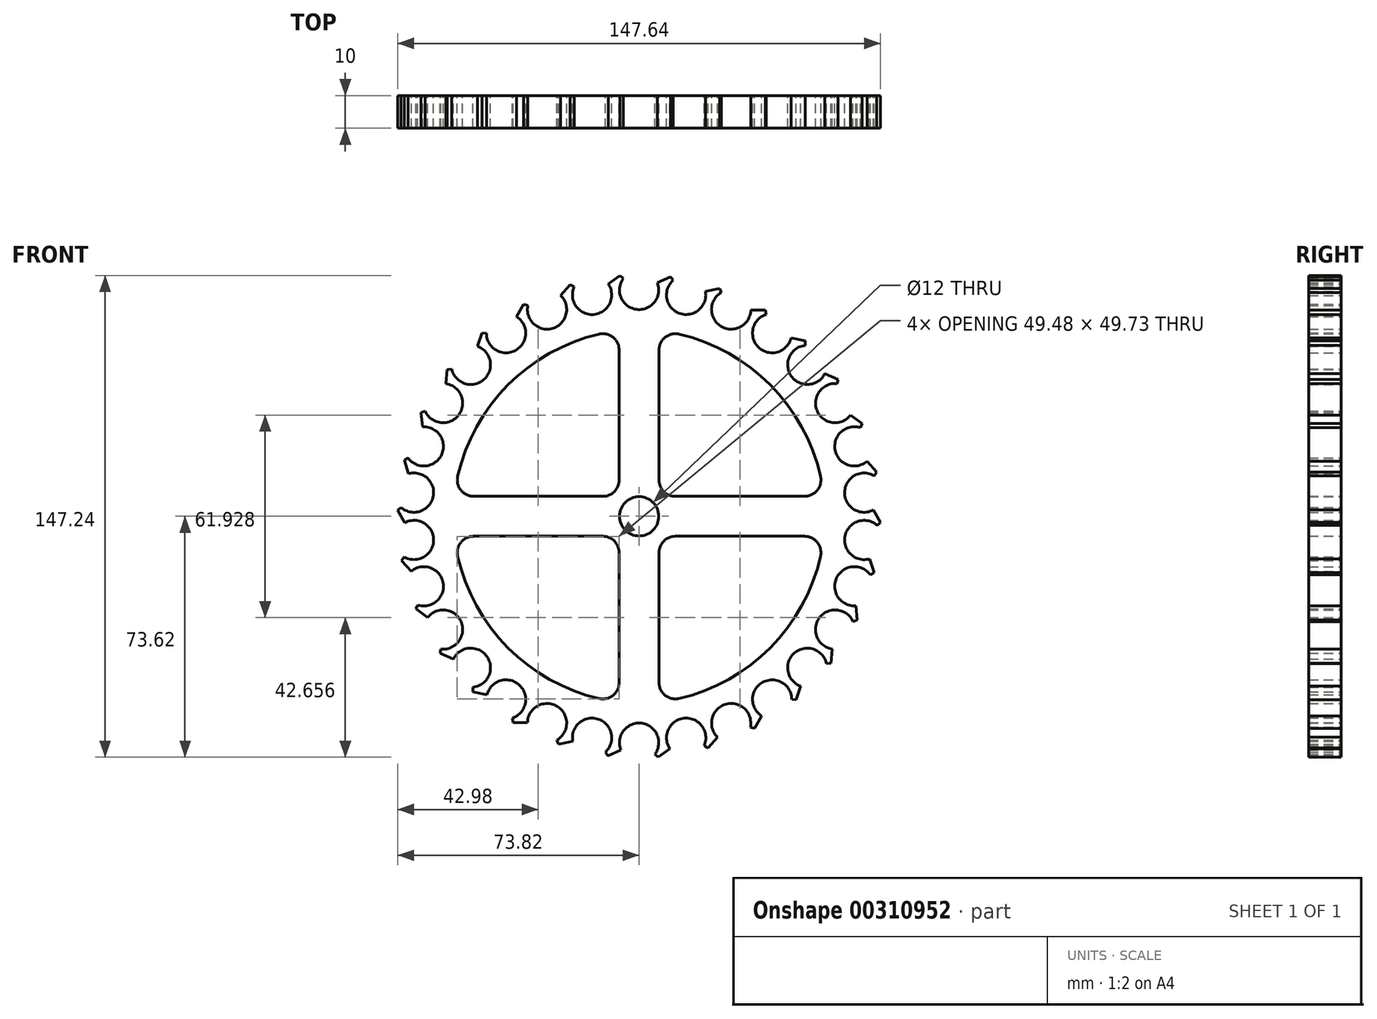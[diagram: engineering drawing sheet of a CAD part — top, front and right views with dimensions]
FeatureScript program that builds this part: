
annotation { "Feature Type Name" : "Feature", "Feature Type Description" : "" }
export const myFeature = defineFeature(function(context is Context, id is Id, definition is map)
    precondition{}
    {
        {
            var Q0;
            Q0=qCreatedBy(makeId("Front.planeOp"),FACE);
            var sketch = newSketch(context, id + "F0", { "sketchPlane" : qUnion([Q0])});
            skArc(sketch, "E0", {"start": v(10.36, 72.14) * mm, "mid": v(8.6, 66.13) * mm, "end": v(13.14, 61.82) * mm});
            skLineSegment(sketch, "E1", {"start": v(10.36, 72.14) * mm, "end": v(9.57, 73.23) * mm});
            skLineSegment(sketch, "E2.trimOffspring", {"start": v(9.57, 73.23) * mm, "end": v(5.57, 71.44) * mm});
            skArc(sketch, "E3.trimOffspring", {"start": v(0, 63.2) * mm, "mid": v(4.97, 65.84) * mm, "end": v(5.57, 71.44) * mm});
            skArc(sketch, "E4.1.0", {"start": v(-13.14, 61.82) * mm, "mid": v(-8.83, 65.44) * mm, "end": v(-9.4, 71.04) * mm});
            skLineSegment(sketch, "E4.1.1", {"start": v(-5.86, 73.62) * mm, "end": v(-9.4, 71.04) * mm});
            skLineSegment(sketch, "E4.1.2", {"start": v(-4.86, 72.72) * mm, "end": v(-5.86, 73.62) * mm});
            skArc(sketch, "E4.1.3", {"start": v(-4.86, 72.72) * mm, "mid": v(-5.34, 66.47) * mm, "end": v(0, 63.2) * mm});
            skArc(sketch, "E4.2.0", {"start": v(-25.7, 57.74) * mm, "mid": v(-22.24, 62.17) * mm, "end": v(-23.97, 67.53) * mm});
            skLineSegment(sketch, "E4.2.1", {"start": v(-21.04, 70.79) * mm, "end": v(-23.97, 67.53) * mm});
            skLineSegment(sketch, "E4.2.2", {"start": v(-19.87, 70.12) * mm, "end": v(-21.04, 70.79) * mm});
            skArc(sketch, "E4.2.3", {"start": v(-19.87, 70.12) * mm, "mid": v(-19.05, 63.9) * mm, "end": v(-13.14, 61.82) * mm});
            skPoint(sketch, "E4.center", {"position": v(0, 0) * mm});
            skArc(sketch, "E5.2.3.0", {"start": v(-37.15, 51.13) * mm, "mid": v(-34.68, 56.19) * mm, "end": v(-37.49, 61.07) * mm});
            skLineSegment(sketch, "E5.4.3.0", {"start": v(-35.3, 64.87) * mm, "end": v(-37.49, 61.07) * mm});
            skLineSegment(sketch, "E5.7.3.0", {"start": v(-34.02, 64.45) * mm, "end": v(-35.3, 64.87) * mm});
            skArc(sketch, "E5.10.3.0", {"start": v(-34.02, 64.45) * mm, "mid": v(-31.92, 58.55) * mm, "end": v(-25.7, 57.74) * mm});
            skArc(sketch, "E5.2.4.0", {"start": v(-46.97, 42.29) * mm, "mid": v(-45.6, 47.75) * mm, "end": v(-49.37, 51.94) * mm});
            skLineSegment(sketch, "E5.4.4.0", {"start": v(-48.01, 56.11) * mm, "end": v(-49.37, 51.94) * mm});
            skLineSegment(sketch, "E5.7.4.0", {"start": v(-46.67, 55.97) * mm, "end": v(-48.01, 56.11) * mm});
            skArc(sketch, "E5.10.4.0", {"start": v(-46.67, 55.97) * mm, "mid": v(-43.4, 50.64) * mm, "end": v(-37.15, 51.13) * mm});
            skArc(sketch, "E5.2.5.0", {"start": v(-54.73, 31.6) * mm, "mid": v(-54.53, 37.23) * mm, "end": v(-59.09, 40.54) * mm});
            skLineSegment(sketch, "E5.4.5.0", {"start": v(-58.63, 44.9) * mm, "end": v(-59.09, 40.54) * mm});
            skLineSegment(sketch, "E5.7.5.0", {"start": v(-57.3, 45.04) * mm, "end": v(-58.63, 44.9) * mm});
            skArc(sketch, "E5.10.5.0", {"start": v(-57.3, 45.04) * mm, "mid": v(-52.97, 40.5) * mm, "end": v(-46.97, 42.29) * mm});
            skArc(sketch, "E5.2.6.0", {"start": v(-60.1, 19.53) * mm, "mid": v(-61.08, 25.08) * mm, "end": v(-66.22, 27.37) * mm});
            skLineSegment(sketch, "E5.4.6.0", {"start": v(-66.68, 31.73) * mm, "end": v(-66.22, 27.37) * mm});
            skLineSegment(sketch, "E5.7.6.0", {"start": v(-65.4, 32.15) * mm, "end": v(-66.68, 31.73) * mm});
            skArc(sketch, "E5.10.6.0", {"start": v(-65.4, 32.15) * mm, "mid": v(-60.24, 28.6) * mm, "end": v(-54.73, 31.6) * mm});
            skArc(sketch, "E5.2.7.0", {"start": v(-62.85, 6.6) * mm, "mid": v(-64.96, 11.83) * mm, "end": v(-70.47, 13) * mm});
            skLineSegment(sketch, "E5.4.7.0", {"start": v(-71.82, 17.18) * mm, "end": v(-70.47, 13) * mm});
            skLineSegment(sketch, "E5.7.7.0", {"start": v(-70.66, 17.85) * mm, "end": v(-71.82, 17.18) * mm});
            skArc(sketch, "E5.10.7.0", {"start": v(-70.66, 17.85) * mm, "mid": v(-64.87, 15.46) * mm, "end": v(-60.1, 19.53) * mm});
            skArc(sketch, "E5.2.8.0", {"start": v(-62.85, -6.6) * mm, "mid": v(-66, -1.94) * mm, "end": v(-71.63, -1.93) * mm});
            skLineSegment(sketch, "E5.4.8.0", {"start": v(-73.82, 1.87) * mm, "end": v(-71.63, -1.93) * mm});
            skLineSegment(sketch, "E5.7.8.0", {"start": v(-72.83, 2.77) * mm, "end": v(-73.82, 1.87) * mm});
            skArc(sketch, "E5.10.8.0", {"start": v(-72.83, 2.77) * mm, "mid": v(-66.66, 1.63) * mm, "end": v(-62.85, 6.6) * mm});
            skArc(sketch, "E5.2.9.0", {"start": v(-60.1, -19.53) * mm, "mid": v(-64.16, -15.62) * mm, "end": v(-69.66, -16.78) * mm});
            skLineSegment(sketch, "E5.4.9.0", {"start": v(-72.6, -13.52) * mm, "end": v(-69.66, -16.78) * mm});
            skLineSegment(sketch, "E5.7.9.0", {"start": v(-71.8, -12.44) * mm, "end": v(-72.6, -13.52) * mm});
            skArc(sketch, "E5.10.9.0", {"start": v(-71.8, -12.44) * mm, "mid": v(-65.55, -12.26) * mm, "end": v(-62.85, -6.6) * mm});
            skArc(sketch, "E5.2.10.0", {"start": v(-54.73, -31.6) * mm, "mid": v(-59.5, -28.61) * mm, "end": v(-64.65, -30.9) * mm});
            skLineSegment(sketch, "E5.4.10.0", {"start": v(-68.2, -28.32) * mm, "end": v(-64.65, -30.9) * mm});
            skLineSegment(sketch, "E5.7.10.0", {"start": v(-67.66, -27.1) * mm, "end": v(-68.2, -28.32) * mm});
            skArc(sketch, "E5.10.10.0", {"start": v(-67.66, -27.1) * mm, "mid": v(-61.57, -25.62) * mm, "end": v(-60.1, -19.53) * mm});
            skArc(sketch, "E5.2.11.0", {"start": v(-46.97, -42.29) * mm, "mid": v(-52.26, -40.36) * mm, "end": v(-56.82, -43.67) * mm});
            skLineSegment(sketch, "E5.4.11.0", {"start": v(-60.82, -41.88) * mm, "end": v(-56.82, -43.67) * mm});
            skLineSegment(sketch, "E5.7.11.0", {"start": v(-60.54, -40.57) * mm, "end": v(-60.82, -41.88) * mm});
            skArc(sketch, "E5.10.11.0", {"start": v(-60.54, -40.57) * mm, "mid": v(-54.9, -37.86) * mm, "end": v(-54.73, -31.6) * mm});
            skArc(sketch, "E5.2.12.0", {"start": v(-37.15, -51.13) * mm, "mid": v(-42.72, -50.34) * mm, "end": v(-46.5, -54.53) * mm});
            skLineSegment(sketch, "E5.4.12.0", {"start": v(-50.79, -53.61) * mm, "end": v(-46.5, -54.53) * mm});
            skLineSegment(sketch, "E5.7.12.0", {"start": v(-50.79, -52.27) * mm, "end": v(-50.79, -53.61) * mm});
            skArc(sketch, "E5.10.12.0", {"start": v(-50.79, -52.27) * mm, "mid": v(-45.82, -48.45) * mm, "end": v(-46.97, -42.29) * mm});
            skArc(sketch, "E5.2.13.0", {"start": v(-25.7, -57.74) * mm, "mid": v(-31.32, -58.13) * mm, "end": v(-34.14, -63) * mm});
            skLineSegment(sketch, "E5.4.13.0", {"start": v(-38.53, -63) * mm, "end": v(-34.14, -63) * mm});
            skLineSegment(sketch, "E5.7.13.0", {"start": v(-38.8, -61.69) * mm, "end": v(-38.53, -63) * mm});
            skArc(sketch, "E5.10.13.0", {"start": v(-38.8, -61.69) * mm, "mid": v(-34.75, -56.92) * mm, "end": v(-37.15, -51.13) * mm});
            skArc(sketch, "E5.2.14.0", {"start": v(-13.14, -61.82) * mm, "mid": v(-18.55, -63.37) * mm, "end": v(-20.3, -68.72) * mm});
            skLineSegment(sketch, "E5.4.14.0", {"start": v(-24.59, -69.63) * mm, "end": v(-20.3, -68.72) * mm});
            skLineSegment(sketch, "E5.7.14.0", {"start": v(-25.14, -68.4) * mm, "end": v(-24.59, -69.63) * mm});
            skArc(sketch, "E5.10.14.0", {"start": v(-25.14, -68.4) * mm, "mid": v(-22.15, -62.9) * mm, "end": v(-25.7, -57.74) * mm});
            skArc(sketch, "E5.2.15.0", {"start": v(0, -63.2) * mm, "mid": v(-4.97, -65.84) * mm, "end": v(-5.57, -71.44) * mm});
            skLineSegment(sketch, "E5.4.15.0", {"start": v(-9.57, -73.23) * mm, "end": v(-5.57, -71.44) * mm});
            skLineSegment(sketch, "E5.7.15.0", {"start": v(-10.36, -72.14) * mm, "end": v(-9.57, -73.23) * mm});
            skArc(sketch, "E5.10.15.0", {"start": v(-10.36, -72.14) * mm, "mid": v(-8.6, -66.13) * mm, "end": v(-13.14, -61.82) * mm});
            skArc(sketch, "E5.2.16.0", {"start": v(13.14, -61.82) * mm, "mid": v(8.83, -65.44) * mm, "end": v(9.4, -71.04) * mm});
            skLineSegment(sketch, "E5.4.16.0", {"start": v(5.86, -73.62) * mm, "end": v(9.4, -71.04) * mm});
            skLineSegment(sketch, "E5.7.16.0", {"start": v(4.86, -72.72) * mm, "end": v(5.86, -73.62) * mm});
            skArc(sketch, "E5.10.16.0", {"start": v(4.86, -72.72) * mm, "mid": v(5.34, -66.47) * mm, "end": v(0, -63.2) * mm});
            skArc(sketch, "E5.2.17.0", {"start": v(25.7, -57.74) * mm, "mid": v(22.24, -62.17) * mm, "end": v(23.97, -67.53) * mm});
            skLineSegment(sketch, "E5.4.17.0", {"start": v(21.04, -70.79) * mm, "end": v(23.97, -67.53) * mm});
            skLineSegment(sketch, "E5.7.17.0", {"start": v(19.87, -70.12) * mm, "end": v(21.04, -70.79) * mm});
            skArc(sketch, "E5.10.17.0", {"start": v(19.87, -70.12) * mm, "mid": v(19.05, -63.9) * mm, "end": v(13.14, -61.82) * mm});
            skArc(sketch, "E5.2.18.0", {"start": v(37.15, -51.13) * mm, "mid": v(34.68, -56.19) * mm, "end": v(37.49, -61.07) * mm});
            skLineSegment(sketch, "E5.4.18.0", {"start": v(35.3, -64.87) * mm, "end": v(37.49, -61.07) * mm});
            skLineSegment(sketch, "E5.7.18.0", {"start": v(34.02, -64.45) * mm, "end": v(35.3, -64.87) * mm});
            skArc(sketch, "E5.10.18.0", {"start": v(34.02, -64.45) * mm, "mid": v(31.92, -58.55) * mm, "end": v(25.7, -57.74) * mm});
            skArc(sketch, "E5.2.19.0", {"start": v(46.97, -42.29) * mm, "mid": v(45.6, -47.75) * mm, "end": v(49.37, -51.94) * mm});
            skLineSegment(sketch, "E5.4.19.0", {"start": v(48.01, -56.11) * mm, "end": v(49.37, -51.94) * mm});
            skLineSegment(sketch, "E5.7.19.0", {"start": v(46.67, -55.97) * mm, "end": v(48.01, -56.11) * mm});
            skArc(sketch, "E5.10.19.0", {"start": v(46.67, -55.97) * mm, "mid": v(43.4, -50.64) * mm, "end": v(37.15, -51.13) * mm});
            skArc(sketch, "E5.2.20.0", {"start": v(54.73, -31.6) * mm, "mid": v(54.53, -37.23) * mm, "end": v(59.09, -40.54) * mm});
            skLineSegment(sketch, "E5.4.20.0", {"start": v(58.63, -44.9) * mm, "end": v(59.09, -40.54) * mm});
            skLineSegment(sketch, "E5.7.20.0", {"start": v(57.3, -45.04) * mm, "end": v(58.63, -44.9) * mm});
            skArc(sketch, "E5.10.20.0", {"start": v(57.3, -45.04) * mm, "mid": v(52.97, -40.5) * mm, "end": v(46.97, -42.29) * mm});
            skArc(sketch, "E5.2.21.0", {"start": v(60.1, -19.53) * mm, "mid": v(61.08, -25.08) * mm, "end": v(66.22, -27.37) * mm});
            skLineSegment(sketch, "E5.4.21.0", {"start": v(66.68, -31.73) * mm, "end": v(66.22, -27.37) * mm});
            skLineSegment(sketch, "E5.7.21.0", {"start": v(65.4, -32.15) * mm, "end": v(66.68, -31.73) * mm});
            skArc(sketch, "E5.10.21.0", {"start": v(65.4, -32.15) * mm, "mid": v(60.24, -28.6) * mm, "end": v(54.73, -31.6) * mm});
            skArc(sketch, "E5.2.22.0", {"start": v(62.85, -6.6) * mm, "mid": v(64.96, -11.83) * mm, "end": v(70.47, -13) * mm});
            skLineSegment(sketch, "E5.4.22.0", {"start": v(71.82, -17.18) * mm, "end": v(70.47, -13) * mm});
            skLineSegment(sketch, "E5.7.22.0", {"start": v(70.66, -17.85) * mm, "end": v(71.82, -17.18) * mm});
            skArc(sketch, "E5.10.22.0", {"start": v(70.66, -17.85) * mm, "mid": v(64.87, -15.46) * mm, "end": v(60.1, -19.53) * mm});
            skArc(sketch, "E5.2.23.0", {"start": v(62.85, 6.6) * mm, "mid": v(66, 1.94) * mm, "end": v(71.63, 1.93) * mm});
            skLineSegment(sketch, "E5.4.23.0", {"start": v(73.82, -1.87) * mm, "end": v(71.63, 1.93) * mm});
            skLineSegment(sketch, "E5.7.23.0", {"start": v(72.83, -2.77) * mm, "end": v(73.82, -1.87) * mm});
            skArc(sketch, "E5.10.23.0", {"start": v(72.83, -2.77) * mm, "mid": v(66.66, -1.63) * mm, "end": v(62.85, -6.6) * mm});
            skArc(sketch, "E5.2.24.0", {"start": v(60.1, 19.53) * mm, "mid": v(64.16, 15.62) * mm, "end": v(69.66, 16.78) * mm});
            skLineSegment(sketch, "E5.4.24.0", {"start": v(72.6, 13.52) * mm, "end": v(69.66, 16.78) * mm});
            skLineSegment(sketch, "E5.7.24.0", {"start": v(71.8, 12.44) * mm, "end": v(72.6, 13.52) * mm});
            skArc(sketch, "E5.10.24.0", {"start": v(71.8, 12.44) * mm, "mid": v(65.55, 12.26) * mm, "end": v(62.85, 6.6) * mm});
            skArc(sketch, "E5.2.25.0", {"start": v(54.73, 31.6) * mm, "mid": v(59.5, 28.61) * mm, "end": v(64.65, 30.9) * mm});
            skLineSegment(sketch, "E5.4.25.0", {"start": v(68.2, 28.32) * mm, "end": v(64.65, 30.9) * mm});
            skLineSegment(sketch, "E5.7.25.0", {"start": v(67.66, 27.1) * mm, "end": v(68.2, 28.32) * mm});
            skArc(sketch, "E5.10.25.0", {"start": v(67.66, 27.1) * mm, "mid": v(61.57, 25.62) * mm, "end": v(60.1, 19.53) * mm});
            skArc(sketch, "E5.2.26.0", {"start": v(46.97, 42.29) * mm, "mid": v(52.26, 40.36) * mm, "end": v(56.82, 43.67) * mm});
            skLineSegment(sketch, "E5.4.26.0", {"start": v(60.82, 41.88) * mm, "end": v(56.82, 43.67) * mm});
            skLineSegment(sketch, "E5.7.26.0", {"start": v(60.54, 40.57) * mm, "end": v(60.82, 41.88) * mm});
            skArc(sketch, "E5.10.26.0", {"start": v(60.54, 40.57) * mm, "mid": v(54.9, 37.86) * mm, "end": v(54.73, 31.6) * mm});
            skArc(sketch, "E5.2.27.0", {"start": v(37.15, 51.13) * mm, "mid": v(42.72, 50.34) * mm, "end": v(46.5, 54.53) * mm});
            skLineSegment(sketch, "E5.4.27.0", {"start": v(50.79, 53.61) * mm, "end": v(46.5, 54.53) * mm});
            skLineSegment(sketch, "E5.7.27.0", {"start": v(50.79, 52.27) * mm, "end": v(50.79, 53.61) * mm});
            skArc(sketch, "E5.10.27.0", {"start": v(50.79, 52.27) * mm, "mid": v(45.82, 48.45) * mm, "end": v(46.97, 42.29) * mm});
            skArc(sketch, "E5.2.28.0", {"start": v(25.7, 57.74) * mm, "mid": v(31.32, 58.13) * mm, "end": v(34.14, 63) * mm});
            skLineSegment(sketch, "E5.4.28.0", {"start": v(38.53, 63) * mm, "end": v(34.14, 63) * mm});
            skLineSegment(sketch, "E5.7.28.0", {"start": v(38.8, 61.69) * mm, "end": v(38.53, 63) * mm});
            skArc(sketch, "E5.10.28.0", {"start": v(38.8, 61.69) * mm, "mid": v(34.75, 56.92) * mm, "end": v(37.15, 51.13) * mm});
            skArc(sketch, "E5.2.29.0", {"start": v(13.14, 61.82) * mm, "mid": v(18.55, 63.37) * mm, "end": v(20.3, 68.72) * mm});
            skLineSegment(sketch, "E5.4.29.0", {"start": v(24.59, 69.63) * mm, "end": v(20.3, 68.72) * mm});
            skLineSegment(sketch, "E5.7.29.0", {"start": v(25.14, 68.4) * mm, "end": v(24.59, 69.63) * mm});
            skArc(sketch, "E5.10.29.0", {"start": v(25.14, 68.4) * mm, "mid": v(22.15, 62.9) * mm, "end": v(25.7, 57.74) * mm});
            skCircle(sketch, "E6", {"center": v(0, 0) * mm, "radius": 6 * mm});
            skSolve(sketch);
        }
        {
            var Q0;
            Q0=makeQuery(id+"F0.imprint","IMPRINT",FACE,{"disambiguationData":[TD([[makeQuery(id+"F0.imprint","IMPRINT",EDGE,{"derivedFrom":sQuery(id+"F0.wireOp",EDGE,"E0")}),-1.0]])]});
            extrude(context, id + "F1", {"entities" : qUnion([Q0]), "depth" : 10 * mm});
        }
        {
            var Q0;
            Q0=qCreatedBy(makeId("Front.planeOp"),FACE);
            var sketch = newSketch(context, id + "F2", { "sketchPlane" : qUnion([Q0])});
            skLineSegment(sketch, "E7", {"start": v(0, 0) * mm, "end": v(0, 72.45) * mm});
            skLineSegment(sketch, "E8", {"start": v(0, 0) * mm, "end": v(-82.84, 0) * mm});
            skArc(sketch, "E9.0", {"start": v(-12.23, 55.7) * mm, "mid": v(-40.1, 40.17) * mm, "end": v(-55.46, 12.2) * mm});
            skLineSegment(sketch, "E10.0", {"start": v(-6.1, 11.1) * mm, "end": v(-6.1, 50.83) * mm});
            skLineSegment(sketch, "E11.0", {"start": v(-11.1, 6.1) * mm, "end": v(-50.58, 6.1) * mm});
            skArc(sketch, "E12.filletArc", {"start": v(-11.1, 6.1) * mm, "mid": v(-7.56, 7.56) * mm, "end": v(-6.1, 11.1) * mm});
            skArc(sketch, "E13.filletArc", {"start": v(-6.1, 50.83) * mm, "mid": v(-7.99, 54.74) * mm, "end": v(-12.23, 55.7) * mm});
            skArc(sketch, "E14.filletArc", {"start": v(-55.46, 12.2) * mm, "mid": v(-54.49, 7.98) * mm, "end": v(-50.58, 6.1) * mm});
            skArc(sketch, "E15.MirrorCS", {"start": v(12.23, 55.7) * mm, "mid": v(40.1, 40.17) * mm, "end": v(55.46, 12.2) * mm});
            skArc(sketch, "E16.MirrorCS", {"start": v(6.1, 50.83) * mm, "mid": v(7.99, 54.74) * mm, "end": v(12.23, 55.7) * mm});
            skLineSegment(sketch, "E17.MirrorCS", {"start": v(6.1, 11.1) * mm, "end": v(6.1, 50.83) * mm});
            skArc(sketch, "E18.MirrorCS", {"start": v(11.1, 6.1) * mm, "mid": v(7.56, 7.56) * mm, "end": v(6.1, 11.1) * mm});
            skLineSegment(sketch, "E19.MirrorCS", {"start": v(11.1, 6.1) * mm, "end": v(50.58, 6.1) * mm});
            skArc(sketch, "E20.MirrorCS", {"start": v(55.46, 12.2) * mm, "mid": v(54.49, 7.98) * mm, "end": v(50.58, 6.1) * mm});
            skLineSegment(sketch, "E21.MirrorCS", {"start": v(-11.1, -6.1) * mm, "end": v(-50.58, -6.1) * mm});
            skArc(sketch, "E22.MirrorCS", {"start": v(-11.1, -6.1) * mm, "mid": v(-7.56, -7.56) * mm, "end": v(-6.1, -11.1) * mm});
            skLineSegment(sketch, "E23.MirrorCS", {"start": v(-6.1, -11.1) * mm, "end": v(-6.1, -50.83) * mm});
            skArc(sketch, "E24.MirrorCS", {"start": v(-6.1, -50.83) * mm, "mid": v(-7.99, -54.74) * mm, "end": v(-12.23, -55.7) * mm});
            skArc(sketch, "E25.MirrorCS", {"start": v(-12.23, -55.7) * mm, "mid": v(-40.1, -40.17) * mm, "end": v(-55.46, -12.2) * mm});
            skArc(sketch, "E26.MirrorCS", {"start": v(-55.46, -12.2) * mm, "mid": v(-54.49, -7.98) * mm, "end": v(-50.58, -6.1) * mm});
            skLineSegment(sketch, "E27.MirrorCS", {"start": v(11.1, -6.1) * mm, "end": v(50.58, -6.1) * mm});
            skArc(sketch, "E28.MirrorCS", {"start": v(11.1, -6.1) * mm, "mid": v(7.56, -7.56) * mm, "end": v(6.1, -11.1) * mm});
            skLineSegment(sketch, "E29.MirrorCS", {"start": v(6.1, -11.1) * mm, "end": v(6.1, -50.83) * mm});
            skArc(sketch, "E30.MirrorCS", {"start": v(6.1, -50.83) * mm, "mid": v(7.99, -54.74) * mm, "end": v(12.23, -55.7) * mm});
            skArc(sketch, "E31.MirrorCS", {"start": v(12.23, -55.7) * mm, "mid": v(40.1, -40.17) * mm, "end": v(55.46, -12.2) * mm});
            skArc(sketch, "E32.MirrorCS", {"start": v(55.46, -12.2) * mm, "mid": v(54.49, -7.98) * mm, "end": v(50.58, -6.1) * mm});
            skSolve(sketch);
        }
        {
            var Q0;
            Q0 = qSketchRegion(id + "F2", true);
            extrude(context, id + "F3", {"entities" : qUnion([Q0]), "operationType" : NewBodyOperationType.REMOVE, "depth" : 25 * mm});
        }
    });
